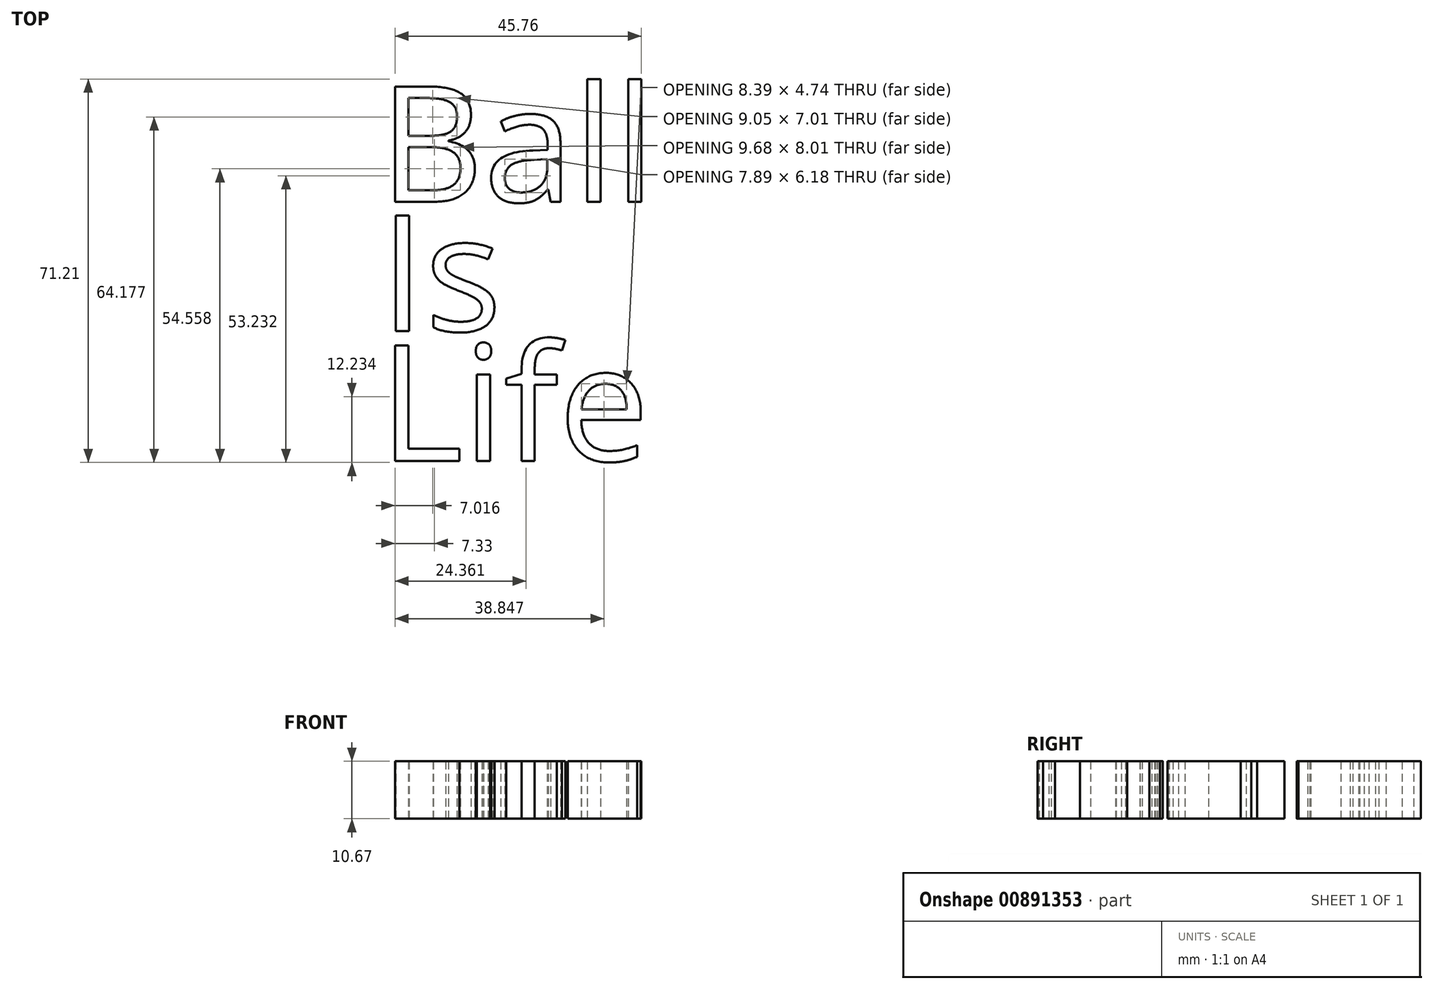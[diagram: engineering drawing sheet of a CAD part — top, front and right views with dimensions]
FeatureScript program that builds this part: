
annotation { "Feature Type Name" : "Feature", "Feature Type Description" : "" }
export const myFeature = defineFeature(function(context is Context, id is Id, definition is map)
    precondition{}
    {
        {
            var Q0;
            Q0=qCreatedBy(makeId("Top.planeOp"),FACE);
            var sketch = newSketch(context, id + "F0", { "sketchPlane" : qUnion([Q0])});
            skText(sketch, "E0", { "text": "Ball", "fontName": "OpenSans-Regular.ttf"});
            const initialGuessF0  = {"E0": [-0.0686, 0.02565, 1, 0, 0.02159]};
            skSetInitialGuess(sketch, initialGuessF0);
            skSolve(sketch);
        }
        {
            var Q0;
            Q0=qCreatedBy(makeId("Top.planeOp"),FACE);
            var sketch = newSketch(context, id + "F1", { "sketchPlane" : qUnion([Q0])});
            skText(sketch, "E1", { "text": "Is\n", "fontName": "OpenSans-Regular.ttf"});
            const initialGuessF1  = {"E1": [-0.06848, 0.00164, 1, 0, 0.0216]};
            skSetInitialGuess(sketch, initialGuessF1);
            skSolve(sketch);
        }
        {
            var Q0;
            Q0=qCreatedBy(makeId("Top.planeOp"),FACE);
            var sketch = newSketch(context, id + "F2", { "sketchPlane" : qUnion([Q0])});
            skText(sketch, "E2", { "text": "Life", "fontName": "OpenSans-Regular.ttf"});
            const initialGuessF2  = {"E2": [-0.06858, -0.02248, 1, 0, 0.02159]};
            skSetInitialGuess(sketch, initialGuessF2);
            skSolve(sketch);
        }
        {
            var Q0;
            Q0 = qSketchRegion(id + "F0", true);
            extrude(context, id + "F3", {"entities" : qUnion([Q0]), "depth" : 10.67 * mm, "offsetDistance" : 25.4 * mm});
        }
        {
            var Q0;
            Q0 = qSketchRegion(id + "F1", true);
            extrude(context, id + "F4", {"entities" : qUnion([Q0]), "depth" : 10.67 * mm, "offsetDistance" : 25.4 * mm});
        }
        {
            var Q0;
            Q0 = qSketchRegion(id + "F2", true);
            extrude(context, id + "F5", {"entities" : qUnion([Q0]), "depth" : 10.67 * mm, "offsetDistance" : 25.4 * mm});
        }
    });
